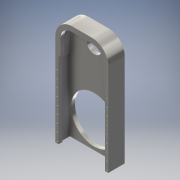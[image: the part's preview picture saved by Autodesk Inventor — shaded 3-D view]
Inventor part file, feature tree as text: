
AUTODESK INVENTOR PART (.ipt)
format: ipt  version: 2016 (Build 200138000, 138)  size: 395,264 bytes
history: native  units: mm
features: sketch x14, extrude x12, reference x8, projected_geometry x7, hole x5, other x1, chamfer x1, plane x1
ambient origin geometry x8: Origin, YZ Plane, XZ Plane, XY Plane, X Axis, Y Axis, Z Axis, Center Point
bodies: Solid1 (feature_tree)
feature tree (49):
  other  "Cup_Dispenser_Slider.ipt"
  sketch  "Sketch2"  dims[d0=10.0mm d1=82.0mm]
  extrude  "Extrusion1"  Depth=82.0mm
  hole  "Hole1"  [1 undecoded]
  extrude  "Extrusion2"  Depth=6.0mm
  chamfer  "Chamfer1"  Distance=6.0mm
  extrude  "Extrusion4"  Depth=19.5mm TaperAngle=0.0deg
  extrude  "Extrusion13"  Depth=2.0mm TaperAngle=45.0deg
  extrude  "Extrusion14"  Depth=3.0mm
  extrude  "Extrusion15"  Depth=6.0mm TaperAngle=0.0deg
  hole  "Hole6"  [1 undecoded]
  extrude  "Extrusion16"  Depth=3.0mm
  extrude  "Extrusion17"  Depth=6.0mm
  extrude  "Extrusion18"  Depth=4.0mm
  hole  "Hole7"  [1 undecoded]
  extrude  "Extrusion9"  Depth=3.0mm TaperAngle=0.0deg
  extrude  "Extrusion10"  Depth=3.0mm TaperAngle=0.0deg
  hole  "Hole3"  [1 undecoded]
  plane  "Work Plane2"
  hole  "Hole4"  [1 undecoded]
  extrude  "Extrusion12"  Depth=3.0mm TaperAngle=0.0deg
  sketch  "Sketch13"  dims[d4=70.0mm d5=70.0mm d6=6.0mm d7=0.0mm]
  sketch  "Sketch4"  dims[d2=117.0mm d3=3.0mm]
  projected_geometry  "Projected Loop1"
  sketch  "Sketch16"  dims[d8=72.0mm d9=19.5mm d10=0.0mm]
  reference  "Reference15"
  reference  "Reference16"
  reference  "Reference17"
  reference  "Reference18"
  reference  "Reference19"
  sketch  "Sketch18"  dims[d13=3.0mm d14=6.0mm d15=4.0mm d16=2.0mm d17=90.0deg d18=4.0mm d19=20.594885mm d20=2.0mm d21=2.0mm d22=45.0deg]
  sketch  "Sketch21"  dims[d23=3.0mm d24=0.0mm d60=31.0mm]
  projected_geometry  "Projected Loop7"
  sketch  "Sketch22"  dims[d61=31.0mm d64=6.0mm d65=0.0mm]
  projected_geometry  "Projected Loop8"
  sketch  "Sketch23"  dims[d66=35.0mm d67=23.0mm]
  projected_geometry  "Projected Loop9"
  sketch  "Sketch24"  dims[d68=3.0mm d69=23.0mm]
  sketch  "Sketch25"  dims[d70=3.0mm d71=0.0mm]
  sketch  "Sketch26"  dims[d72=3.0mm d73=6.0mm d74=4.0mm d75=2.0mm d76=90.0deg d77=4.0mm d78=20.594885mm d81=6.0mm]
  projected_geometry  "Projected Loop10"
  sketch  "Sketch28"  dims[d82=3.0mm d83=6.0mm d84=4.0mm d85=2.0mm d86=90.0deg d87=4.0mm d88=20.594885mm d96=24.0mm]
  reference  "Reference27"
  reference  "Reference28"
  sketch  "Sketch29"  dims[d97=48.0mm d99=2.0mm d100=0.0mm]
  sketch  "Sketch30"  dims[d101=6.0mm d102=0.0mm d103=3.0mm d104=0.0mm d105=3.0mm d106=0.0mm d107=31.0mm d108=31.0mm d109=3.0mm d110=6.0mm d111=4.0mm d112=2.0mm d113=90.0deg d114=4.0mm d115=20.594885mm d116=3.0mm d117=0.0mm d123=3.0mm d124=0.0mm d125=60.0mm d126=30.0mm d127=3.0mm d128=2.0mm d129=0.0mm d130=3.0mm d131=90.0mm d133=12.0mm d134=10.0mm d136=10.0mm d138=2.0mm d139=6.0mm d140=4.0mm d141=2.0mm d142=90.0deg d143=4.0mm d144=20.594885mm d152=5.0mm d158=3.0mm d161=45.0deg d162=45.0deg]
  projected_geometry  "Projected Loop12"
  reference  "Reference34"
  projected_geometry  "Projected Loop15"
note: 5 required parameter values undecoded (feature->parameter linkage not recoverable at this tier; creation-order binding heuristic only, values carry confidence <= 0.55)
